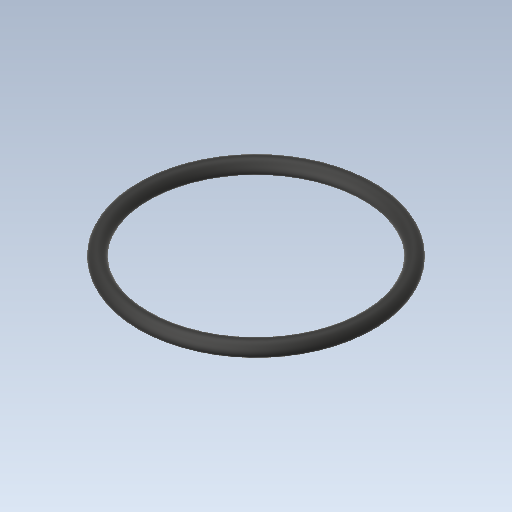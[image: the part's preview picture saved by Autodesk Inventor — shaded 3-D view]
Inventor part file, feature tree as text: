
AUTODESK INVENTOR PART (.ipt)
format: ipt  version: 2020 (Build 240168000, 168)  size: 123,392 bytes
history: native  units: in
note: dims shown in document units (in); Inventor stores cm internally (conversion verified against a paired STEP export)
features: revolve x1, sketch x1
ambient origin geometry x8: Origin, YZ Plane, XZ Plane, XY Plane, X Axis, Y Axis, Z Axis, Center Point
bodies: Solid1 (feature_tree)
feature tree (2):
  revolve  "Revolution1"  [1 undecoded]
  sketch  "Sketch1"  dims[d0=0.07in d1=0.5295in d2=90.0deg]
note: 1 required parameter value undecoded (feature->parameter linkage not recoverable at this tier; creation-order binding heuristic only, values carry confidence <= 0.55)
